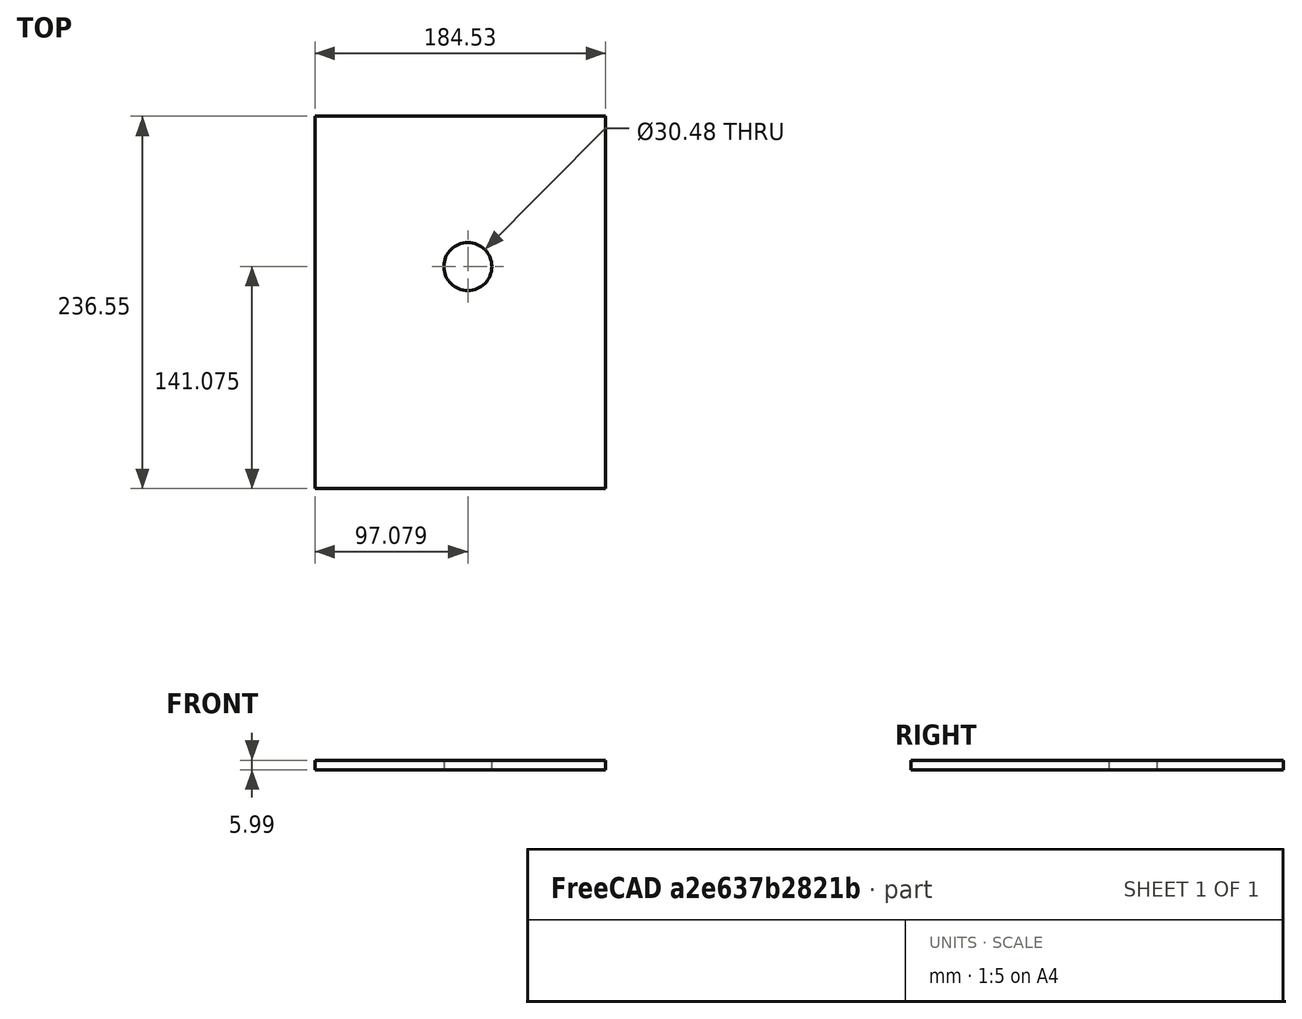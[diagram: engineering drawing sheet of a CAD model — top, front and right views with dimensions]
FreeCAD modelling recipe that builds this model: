
FCSTD DOCUMENT  (FreeCAD 0.19R24267 (Git))
Label: Inv1-P3
License: All rights reserved
LicenseURL: http://en.wikipedia.org/wiki/All_rights_reserved
objects: TechDraw::DrawViewDimension×6, TechDraw::DrawProjGroupItem×2, TechDraw::DrawHatch×2, TechDraw::DrawViewAnnotation×2, Sketcher::SketchObject×1, Part::Extrusion×1, TechDraw::DrawSVGTemplate×1, TechDraw::DrawProjGroup×1, TechDraw::DrawPage×1
note: 2 computed .brp shape members not serialized (recipe doc carries the construction recipe); baked Part::Feature solids carry a one-line shape summary decoded from their .brp

FEATURE [Sketcher::SketchObject] Sketch
  FullyConstrained = false
  sketch-geometry (5):
    g0: LineSegment StartX=-58.0601 StartY=142.494 StartZ=0 EndX=126.471 EndY=142.494 EndZ=0
    g1: LineSegment StartX=126.471 StartY=142.494 StartZ=0 EndX=126.471 EndY=-94.0562 EndZ=0
    g2: LineSegment StartX=126.471 StartY=-94.0562 StartZ=0 EndX=-58.0601 EndY=-94.0562 EndZ=0
    g3: LineSegment StartX=-58.0601 StartY=-94.0562 StartZ=0 EndX=-58.0601 EndY=142.494 EndZ=0
    g4: Circle CenterX=39.0187 CenterY=47.0154 CenterZ=0 NormalX=0 NormalY=0 NormalZ=1 AngleXU=0 Radius=15.24
  constraints (13):
    c: Coincident(g0,g1)
    c: Coincident(g1,g2)
    c: Coincident(g2,g3)
    c: Coincident(g3,g0)
    c: Horizontal(g0)
    c: Horizontal(g2)
    c: Vertical(g1)
    c: Vertical(g3)
    c: DistanceX(g0,g0) = 184.531
    c: DistanceY(g3,g3) = 236.55
    c: Distance(g4,g0) = 95.4786
    c: Distance(g4,g3) = 97.0788
    c: Diameter(g4) = 30.48
FEATURE [Part::Extrusion] Extrude
  Base = -> Sketch
  Dir = (0,0,1)
  DirMode = 2
  FaceMakerClass = Part::FaceMakerBullseye
  LengthFwd = 5.9944
  LengthRev = 0
  Solid = true
  Symmetric = false
FEATURE [TechDraw::DrawSVGTemplate] Template
  Height = 215.9
  Orientation = 1
  Width = 279.4
FEATURE [TechDraw::DrawProjGroupItem] ProjItem  label="Front"
  CoarseView = false
  Direction = (0,0,1)
  Focus = 100
  HardHidden = false
  IsoCount = 0
  IsoHidden = false
  IsoVisible = false
  LockPosition = true
  Perspective = false
  Rotation = 0
  RotationVector = (1,0,0)
  Scale = 0.5
  ScaleType = 2
  SeamHidden = false
  SeamVisible = true
  SmoothHidden = false
  SmoothVisible = true
  Source = -> [Extrude]
  Type = 0
  X = 0
  XDirection = (1,0,0)
  Y = 0
FEATURE [TechDraw::DrawProjGroupItem] ProjItem001  label="Left"
  CoarseView = false
  Direction = (-1,0,1e-16)
  Focus = 100
  HardHidden = false
  IsoCount = 0
  IsoHidden = false
  IsoVisible = false
  LockPosition = false
  Perspective = false
  Rotation = 0
  RotationVector = (1,0,0)
  Scale = 0.5
  ScaleType = 2
  SeamHidden = false
  SeamVisible = true
  SmoothHidden = false
  SmoothVisible = true
  Source = -> [Extrude]
  Type = 1
  X = 87.6134
  XDirection = (1e-16,0,1)
  Y = 0
FEATURE [TechDraw::DrawProjGroup] ProjGroup
  Anchor = -> ProjItem
  AutoDistribute = true
  LockPosition = false
  ProjectionType = 0
  Rotation = 0
  Scale = 0.5
  ScaleType = 0
  Source = -> [Extrude]
  Views = -> [ProjItem,ProjItem001]
  X = 127.347
  Y = 107.244
  spacingX = 15.0114
  spacingY = 15.0114
FEATURE [TechDraw::DrawHatch] Hatch  label="HatchF0"
  HatchPattern = <path>
  Source = -> ProjItem [Face0]
FEATURE [TechDraw::DrawHatch] Hatch001  label="Hatch001F0"
  HatchPattern = <path>
  Source = -> ProjItem001 [Face0]
FEATURE [TechDraw::DrawViewAnnotation] Annotation
  Font = osifont
  LineSpace = 80
  LockPosition = false
  MaxWidth = -1
  Rotation = 0
  ScaleType = 0
  Text = Figure S1 (Inverted 1) | Panel 3 [camera port] | Quantity: 1
  TextSize = 5.0038
  TextStyle = 0
  X = 32.3295
  Y = 195.58
FEATURE [TechDraw::DrawViewAnnotation] Annotation002
  Font = osifont
  LineSpace = 80
  LockPosition = false
  MaxWidth = -1
  Rotation = 0
  ScaleType = 0
  Text = Units: Inches
  TextSize = 5.0038
  TextStyle = 0
  X = 259.08
  Y = 5.08
FEATURE [TechDraw::DrawViewDimension] Dimension
  Arbitrary = false
  ArbitraryTolerances = false
  EqualTolerance = true
  FormatSpec = %.3f
  FormatSpecOverTolerance = %+.3f
  FormatSpecUnderTolerance = %+.3f
  Inverted = false
  LockPosition = false
  MeasureType = 1
  OverTolerance = 0
  References2D = -> [ProjItem]
  Rotation = 0
  ScaleType = 0
  TheoreticalExact = false
  Type = 1
  UnderTolerance = 0
  X = 26.1492
  Y = -0.415822
FEATURE [TechDraw::DrawViewDimension] Dimension001
  Arbitrary = false
  ArbitraryTolerances = false
  EqualTolerance = true
  FormatSpec = %.3f
  FormatSpecOverTolerance = %+.3f
  FormatSpecUnderTolerance = %+.3f
  Inverted = false
  LockPosition = false
  MeasureType = 1
  OverTolerance = 0
  References2D = -> [ProjItem]
  Rotation = 0
  ScaleType = 0
  TheoreticalExact = false
  Type = 2
  UnderTolerance = 0
  X = -17.194
  Y = 36.3419
FEATURE [TechDraw::DrawViewDimension] Dimension002
  Arbitrary = false
  ArbitraryTolerances = false
  EqualTolerance = true
  FormatSpec = ⌀%.3f
  FormatSpecOverTolerance = %+.3f
  FormatSpecUnderTolerance = %+.3f
  Inverted = false
  LockPosition = false
  MeasureType = 1
  OverTolerance = 0
  References2D = -> [ProjItem]
  Rotation = 0
  ScaleType = 0
  TheoreticalExact = false
  Type = 5
  UnderTolerance = 0
  X = 17.9896
  Y = 33.2942
FEATURE [TechDraw::DrawViewDimension] Dimension003
  Arbitrary = false
  ArbitraryTolerances = false
  EqualTolerance = true
  FormatSpec = %.3f
  FormatSpecOverTolerance = %+.3f
  FormatSpecUnderTolerance = %+.3f
  Inverted = false
  LockPosition = false
  MeasureType = 1
  OverTolerance = 0
  References2D = -> [ProjItem]
  Rotation = 0
  ScaleType = 0
  TheoreticalExact = false
  Type = 1
  UnderTolerance = 0
  X = 0.268502
  Y = 70.4146
FEATURE [TechDraw::DrawViewDimension] Dimension004
  Arbitrary = false
  ArbitraryTolerances = false
  EqualTolerance = true
  FormatSpec = %.3f
  FormatSpecOverTolerance = %+.3f
  FormatSpecUnderTolerance = %+.3f
  Inverted = false
  LockPosition = false
  MeasureType = 1
  OverTolerance = 0
  References2D = -> [ProjItem]
  Rotation = 0
  ScaleType = 0
  TheoreticalExact = false
  Type = 2
  UnderTolerance = 0
  X = 60.6318
  Y = 1.34251
FEATURE [TechDraw::DrawViewDimension] Dimension005
  Arbitrary = false
  ArbitraryTolerances = false
  EqualTolerance = true
  FormatSpec = %.3f
  FormatSpecOverTolerance = %+.3f
  FormatSpecUnderTolerance = %+.3f
  Inverted = false
  LockPosition = false
  MeasureType = 1
  OverTolerance = 0
  References2D = -> [ProjItem001]
  Rotation = 0
  ScaleType = 0
  TheoreticalExact = false
  Type = 1
  UnderTolerance = 0
  X = 18.2581
  Y = 30.1394
FEATURE [TechDraw::DrawPage] Page
  KeepUpdated = true
  NextBalloonIndex = 1
  ProjectionType = 0
  Template = -> Template
  Views = -> [ProjGroup,Annotation,Annotation002,Dimension,Dimension001,Dimension002,Dimension003,Dimension004,Dimension005]
note: 2 file-system paths scrubbed to <path> (originals preserved in the JSON sidecar)
